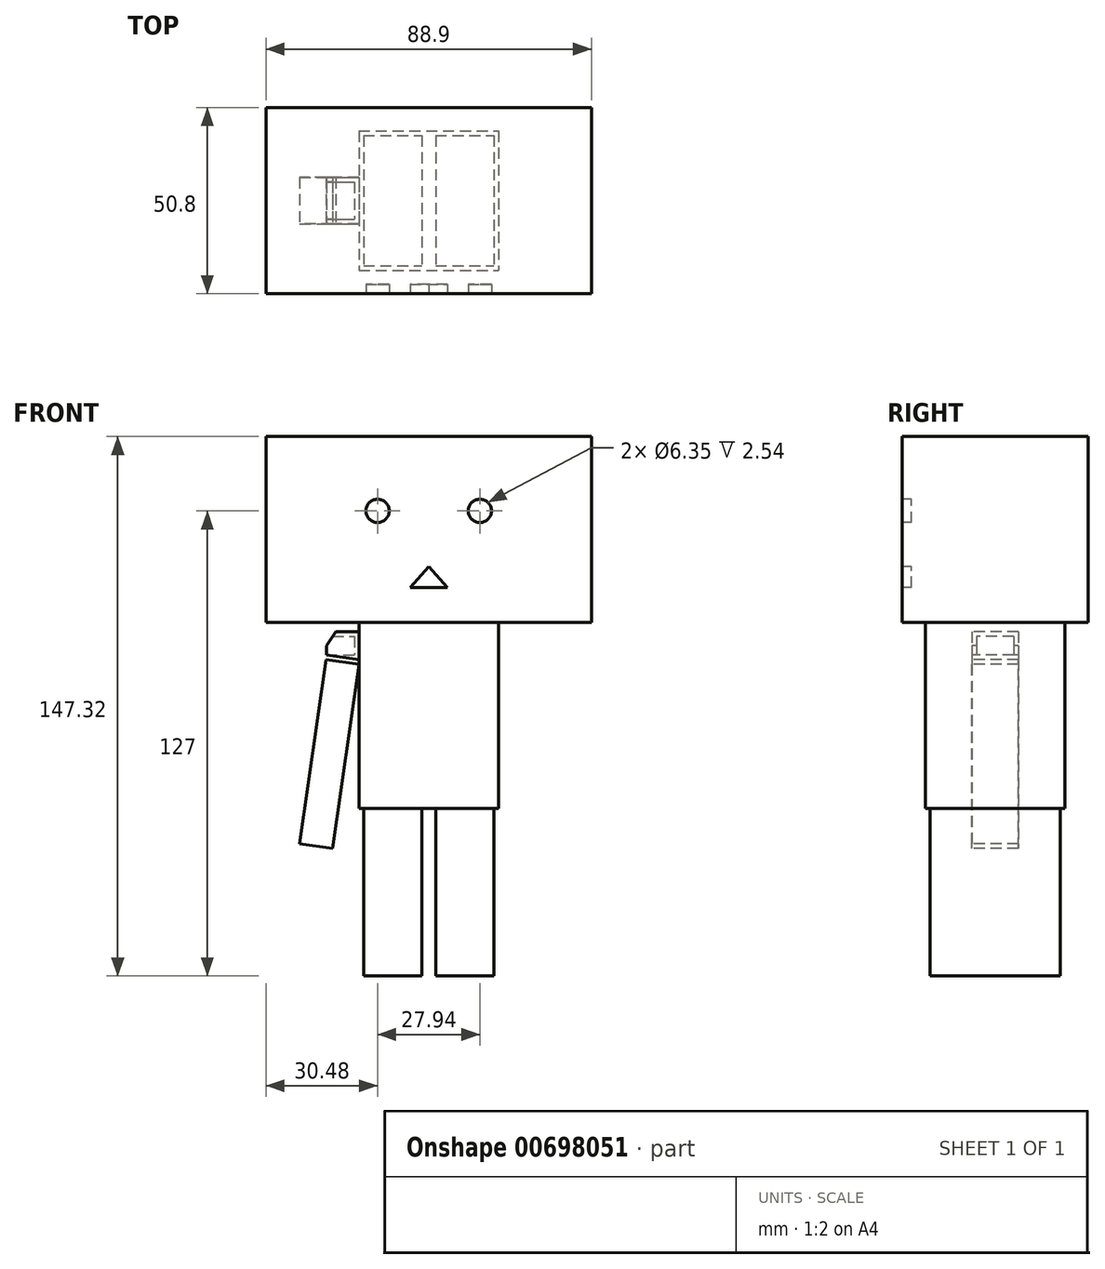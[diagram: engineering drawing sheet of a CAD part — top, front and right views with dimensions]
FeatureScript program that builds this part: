
annotation { "Feature Type Name" : "Feature", "Feature Type Description" : "" }
export const myFeature = defineFeature(function(context is Context, id is Id, definition is map)
    precondition{}
    {
        {
            var Q0;
            Q0=qCreatedBy(makeId("Front.planeOp"),FACE);
            var sketch = newSketch(context, id + "F0", { "sketchPlane" : qUnion([Q0])});
            skLineSegment(sketch, "E0.bottom", {"start": v(0, 0) * mm, "end": v(88.9, 0) * mm});
            skLineSegment(sketch, "E0.top", {"start": v(0, 50.8) * mm, "end": v(88.9, 50.8) * mm});
            skLineSegment(sketch, "E0.left", {"start": v(0, 0) * mm, "end": v(0, 50.8) * mm});
            skLineSegment(sketch, "E0.right", {"start": v(88.9, 0) * mm, "end": v(88.9, 50.8) * mm});
            skSolve(sketch);
        }
        {
            var Q0;
            Q0 = qSketchRegion(id + "F0", true);
            extrude(context, id + "F1", {"entities" : qUnion([Q0]), "depth" : 50.8 * mm, "offsetDistance" : 25.4 * mm});
        }
        {
            var Q0;
            Q0=makeQuery(id+"F1.opExtrude","SWEPT_FACE",FACE,{"disambiguationData":[OSD([sQuery(id+"F0.wireOp",EDGE,"E0.top")])]});
            var sketch = newSketch(context, id + "F2", { "sketchPlane" : qUnion([Q0])});
            skLineSegment(sketch, "E1", {"start": v(0, -25.4) * mm, "end": v(88.9, -25.4) * mm});
            skSolve(sketch);
        }
        {
            var Q0;
            Q0=makeQuery(id+"F1.opExtrude","CAP_FACE",FACE,{"disambiguationData":[OSD([sQuery(id+"F0.wireOp",EDGE,"E0.bottom"),sQuery(id+"F0.wireOp",EDGE,"E0.top"),sQuery(id+"F0.wireOp",EDGE,"E0.left"),sQuery(id+"F0.wireOp",EDGE,"E0.right")])],"isStart":false});
            var sketch = newSketch(context, id + "F3", { "sketchPlane" : qUnion([Q0])});
            skCircle(sketch, "E2", {"center": v(30.48, 30.48) * mm, "radius": 3.18 * mm});
            skCircle(sketch, "E3", {"center": v(58.42, 30.48) * mm, "radius": 3.18 * mm});
            skLineSegment(sketch, "E4", {"start": v(44.45, 15.24) * mm, "end": v(39.37, 9.56) * mm});
            skLineSegment(sketch, "E5", {"start": v(39.37, 9.56) * mm, "end": v(49.53, 9.56) * mm});
            skLineSegment(sketch, "E6", {"start": v(49.53, 9.56) * mm, "end": v(44.45, 15.24) * mm});
            skSolve(sketch);
        }
        {
            var Q0;
            Q0 = qSketchRegion(id + "F3", true);
            extrude(context, id + "F4", {"entities" : qUnion([Q0]), "operationType" : NewBodyOperationType.REMOVE, "oppositeDirection" : true, "depth" : 2.54 * mm, "offsetDistance" : 25.4 * mm});
        }
        {
            var Q0;
            Q0=makeQuery(id+"F1.opExtrude","SWEPT_FACE",FACE,{"disambiguationData":[OSD([sQuery(id+"F0.wireOp",EDGE,"E0.bottom")])]});
            var sketch = newSketch(context, id + "F5", { "sketchPlane" : qUnion([Q0])});
            skLineSegment(sketch, "E7.bottom", {"start": v(25.4, 6.35) * mm, "end": v(63.5, 6.35) * mm});
            skLineSegment(sketch, "E7.top", {"start": v(25.4, 44.45) * mm, "end": v(63.5, 44.45) * mm});
            skLineSegment(sketch, "E7.left", {"start": v(25.4, 6.35) * mm, "end": v(25.4, 44.45) * mm});
            skLineSegment(sketch, "E7.right", {"start": v(63.5, 6.35) * mm, "end": v(63.5, 44.45) * mm});
            skSolve(sketch);
        }
        {
            var Q0;
            Q0=makeQuery(id+"F5.imprint","IMPRINT",FACE,{"disambiguationData":[TD([[makeQuery(id+"F5.imprint","IMPRINT",EDGE,{"derivedFrom":sQuery(id+"F5.wireOp",EDGE,"E7.bottom")}),1.0]])]});
            extrude(context, id + "F6", {"entities" : qUnion([Q0]), "depth" : 50.8 * mm, "offsetDistance" : 25.4 * mm});
        }
        {
            var Q0;
            Q0=makeQuery(id+"F6.opExtrude","CAP_FACE",FACE,{"disambiguationData":[OSD([sQuery(id+"F5.wireOp",EDGE,"E7.bottom"),sQuery(id+"F5.wireOp",EDGE,"E7.top"),sQuery(id+"F5.wireOp",EDGE,"E7.left"),sQuery(id+"F5.wireOp",EDGE,"E7.right")])],"isStart":false});
            var sketch = newSketch(context, id + "F7", { "sketchPlane" : qUnion([Q0])});
            skLineSegment(sketch, "E8.bottom", {"start": v(26.67, 7.62) * mm, "end": v(42.54, 7.62) * mm});
            skLineSegment(sketch, "E8.top", {"start": v(26.67, 43.18) * mm, "end": v(42.54, 43.18) * mm});
            skLineSegment(sketch, "E8.left", {"start": v(26.67, 7.62) * mm, "end": v(26.67, 43.18) * mm});
            skLineSegment(sketch, "E8.right", {"start": v(42.54, 7.62) * mm, "end": v(42.54, 43.18) * mm});
            skLineSegment(sketch, "E9.bottom", {"start": v(46.35, 7.62) * mm, "end": v(62.23, 7.62) * mm});
            skLineSegment(sketch, "E9.top", {"start": v(46.35, 43.18) * mm, "end": v(62.23, 43.18) * mm});
            skLineSegment(sketch, "E9.left", {"start": v(46.35, 7.62) * mm, "end": v(46.35, 43.18) * mm});
            skLineSegment(sketch, "E9.right", {"start": v(62.23, 7.62) * mm, "end": v(62.23, 43.18) * mm});
            skSolve(sketch);
        }
        {
            var Q0;
            Q0 = qSketchRegion(id + "F7", true);
            extrude(context, id + "F8", {"entities" : qUnion([Q0]), "depth" : 45.72 * mm, "offsetDistance" : 25.4 * mm});
        }
        {
            var Q0;
            Q0=makeQuery(id+"F6.opExtrude","SWEPT_FACE",FACE,{"disambiguationData":[OSD([sQuery(id+"F5.wireOp",EDGE,"E7.left")])]});
            var sketch = newSketch(context, id + "F9", { "sketchPlane" : qUnion([Q0])});
            skLineSegment(sketch, "E10.bottom", {"start": v(19.05, -2.54) * mm, "end": v(31.75, -2.54) * mm});
            skLineSegment(sketch, "E10.top", {"start": v(19.05, -10.16) * mm, "end": v(31.75, -10.16) * mm});
            skLineSegment(sketch, "E10.left", {"start": v(19.05, -2.54) * mm, "end": v(19.05, -10.16) * mm});
            skLineSegment(sketch, "E10.right", {"start": v(31.75, -2.54) * mm, "end": v(31.75, -10.16) * mm});
            skSolve(sketch);
        }
        {
            var Q0;
            Q0 = qSketchRegion(id + "F9", true);
            extrude(context, id + "F10", {"entities" : qUnion([Q0]), "depth" : 8.9 * mm, "offsetDistance" : 25.4 * mm});
        }
        {
            var Q0;
            Q0=makeQuery(id+"F10.opExtrude","CAP_FACE",FACE,{"disambiguationData":[OSD([sQuery(id+"F9.wireOp",EDGE,"E10.bottom"),sQuery(id+"F9.wireOp",EDGE,"E10.top"),sQuery(id+"F9.wireOp",EDGE,"E10.left"),sQuery(id+"F9.wireOp",EDGE,"E10.right")])],"isStart":false});
            shell(context, id + "F11", {"entities" : qUnion([Q0]), "thickness" : 1.27 * mm});
        }
        {
            var Q0;
            Q0=makeQuery(id+"F10.opExtrude","SWEPT_FACE",FACE,{"disambiguationData":[OSD([sQuery(id+"F9.wireOp",EDGE,"E10.right")])]});
            var sketch = newSketch(context, id + "F12", { "sketchPlane" : qUnion([Q0])});
            skLineSegment(sketch, "E11", {"start": v(19.05, -2.54) * mm, "end": v(16.5, -6.35) * mm});
            skLineSegment(sketch, "E12", {"start": v(16.5, -6.35) * mm, "end": v(16.5, -2.54) * mm});
            skLineSegment(sketch, "E13", {"start": v(16.5, -2.54) * mm, "end": v(19.05, -2.54) * mm});
            skLineSegment(sketch, "E14", {"start": v(16.5, -8.9) * mm, "end": v(25.4, -10.16) * mm});
            skLineSegment(sketch, "E15", {"start": v(25.4, -10.16) * mm, "end": v(16.5, -10.16) * mm});
            skLineSegment(sketch, "E16", {"start": v(16.5, -10.16) * mm, "end": v(16.5, -8.9) * mm});
            skSolve(sketch);
        }
        {
            var Q0;
            Q0 = qSketchRegion(id + "F12", true);
            extrude(context, id + "F13", {"entities" : qUnion([Q0]), "operationType" : NewBodyOperationType.REMOVE, "oppositeDirection" : true, "depth" : 25.4 * mm, "offsetDistance" : 25.4 * mm});
        }
        {
            var Q0;
            Q0=makeQuery(id+"F10.opExtrude","SWEPT_FACE",FACE,{"disambiguationData":[OSD([sQuery(id+"F9.wireOp",EDGE,"E10.right")])]});
            var sketch = newSketch(context, id + "F14", { "sketchPlane" : qUnion([Q0])});
            skLineSegment(sketch, "E17", {"start": v(16.42, -10.16) * mm, "end": v(25.4, -11.44) * mm});
            skLineSegment(sketch, "E18", {"start": v(25.4, -11.44) * mm, "end": v(18.22, -61.73) * mm});
            skLineSegment(sketch, "E19", {"start": v(18.22, -61.73) * mm, "end": v(9.24, -60.45) * mm});
            skLineSegment(sketch, "E20", {"start": v(9.24, -60.45) * mm, "end": v(16.42, -10.16) * mm});
            skSolve(sketch);
        }
        {
            var Q0;
            Q0 = qSketchRegion(id + "F14", true);
            var Q1;
            Q1=makeQuery(id+"F10.opExtrude","SWEPT_FACE",FACE,{"disambiguationData":[OSD([sQuery(id+"F9.wireOp",EDGE,"E10.left")])]});
            extrude(context, id + "F15", {"entities" : qUnion([Q0]), "endBound" : BoundingType.UP_TO_SURFACE, "oppositeDirection" : true, "depth" : 25.4 * mm, "endBoundEntityFace" : qUnion([Q1]), "offsetDistance" : 25.4 * mm});
        }
    });
